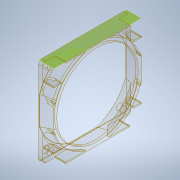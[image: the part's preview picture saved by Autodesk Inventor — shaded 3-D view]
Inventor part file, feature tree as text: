
AUTODESK INVENTOR PART (.ipt)
format: ipt  version: 2022.1 (Build 261234000, 234)  size: 620,032 bytes
history: native  units: in
note: dims shown in document units (in); Inventor stores cm internally (conversion verified against a paired STEP export)
features: other x3, extrude x1, sketch x1
ambient origin geometry x8: Origin, YZ Plane, XZ Plane, XY Plane, X Axis, Y Axis, Z Axis, Center Point
bodies: Solid1 (feature_tree)
feature tree (5):
  other  "Repaired Geometry1"
  extrude  "Extrusion1"  [1 undecoded]
  sketch  "Sketch1"  dims[d0=0.0039in d1=0.0in]
  other  "Composite1"
  other  "Srf1"
note: 1 required parameter value undecoded (feature->parameter linkage not recoverable at this tier; creation-order binding heuristic only, values carry confidence <= 0.55)
